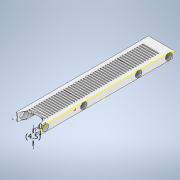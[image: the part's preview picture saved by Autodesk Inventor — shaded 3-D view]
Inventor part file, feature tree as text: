
AUTODESK INVENTOR PART (.ipt)
format: ipt  version: 2022.1 (Build 261234000, 234)  size: 492,544 bytes
history: native  units: mm
features: extrude x7, sketch x7, projected_geometry x1
ambient origin geometry x8: Origin, YZ Plane, XZ Plane, XY Plane, X Axis, Y Axis, Z Axis, Center Point
bodies: Solid1 (feature_tree)
feature tree (15):
  extrude  "Extrusion1"  Depth=155.0mm
  extrude  "Extrusion2"  Depth=150.0mm
  extrude  "Extrusion3"  Depth=9.0mm TaperAngle=0.0deg
  sketch  "Sketch5"  dims[d7=2.0mm d8=480.0mm d10=3.02mm d11=10.0mm d13=10.0mm]
  extrude  "Extrusion6"  Depth=10.0mm
  extrude  "Insert_Holes"  Depth=5.0mm
  extrude  "Extrusion11"  Depth=2.0mm
  extrude  "Extrusion12"  Depth=5.0mm
  sketch  "Sketch1"  dims[d0=30.0mm d1=155.0mm]
  sketch  "Sketch2"  dims[d2=20.0mm d3=150.0mm]
  projected_geometry  "Projected Loop1"
  sketch  "Sketch3"  dims[d4=2.5mm d5=9.0mm d6=0.0mm]
  sketch  "Sketch7"  dims[d15=3.0mm d16=0.0mm d17=5.0mm]
  sketch  "Sketch12"  dims[d18=1.5mm d19=2.0mm]
  sketch  "Sketch13"  dims[d20=37.13mm d21=1.5mm d22=67.55mm d23=1.5mm d24=8.0mm d25=16.0mm d26=0.0mm d38=0.0mm d39=4.5mm d43=5.0mm d45=37.13mm d47=67.55mm d49=47.31mm d51=8.0mm d52=8.0mm d53=8.0mm d54=8.0mm d55=16.0mm d56=0.0mm d58=5.0mm d59=37.13mm d60=47.31mm d61=67.55mm d62=10.0mm d63=0.0mm d65=30.0mm d67=3.2mm d68=10.0mm d70=10.0mm d84=25.4mm d85=10.0mm d86=0.0mm d87=1.5mm d88=1.0mm d89=4.5mm d90=4.5mm d91=1.0mm d92=5.0mm d93=0.0mm]
